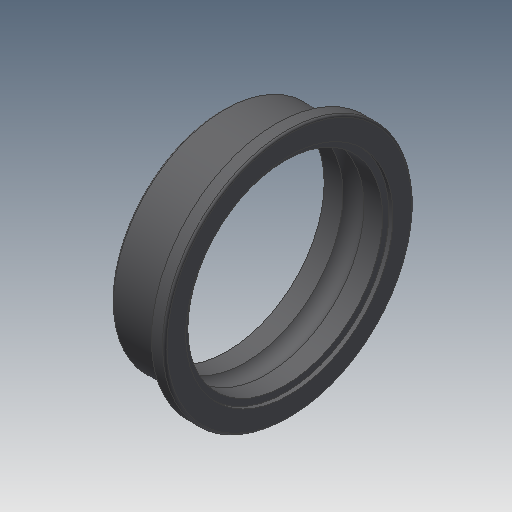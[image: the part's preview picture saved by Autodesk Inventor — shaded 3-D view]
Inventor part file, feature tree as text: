
AUTODESK INVENTOR PART (.ipt)
format: ipt  version: 2019.4 (Build 234330000, 330)  size: 182,784 bytes
history: native  units: mm
features: other x14, revolve x1, sketch x1
ambient origin geometry x8: Origin, YZ Plane, XZ Plane, XY Plane, X Axis, Y Axis, Z Axis, Center Point
bodies: Solid1 (feature_tree)
feature tree (16):
  revolve  "Revolution1"  [1 undecoded]
  other  "ip_st_1_XY"
  other  "ip_st_1_YZ"
  other  "ip_st_1_ZX"
  other  "ip_st_1_X"
  other  "ip_st_1_Y"
  other  "ip_st_1_Z"
  other  "ip_st_1_Center"
  other  "ip_st_2_XY"
  other  "ip_st_2_YZ"
  other  "ip_st_2_ZX"
  other  "ip_st_2_X"
  other  "ip_st_2_Y"
  other  "ip_st_2_Z"
  other  "ip_st_2_Center"
  sketch  "Sketch_1"  dims[d0=360.0deg d1=0.0mm d2=0.0mm]
note: 1 required parameter value undecoded (feature->parameter linkage not recoverable at this tier; creation-order binding heuristic only, values carry confidence <= 0.55)
